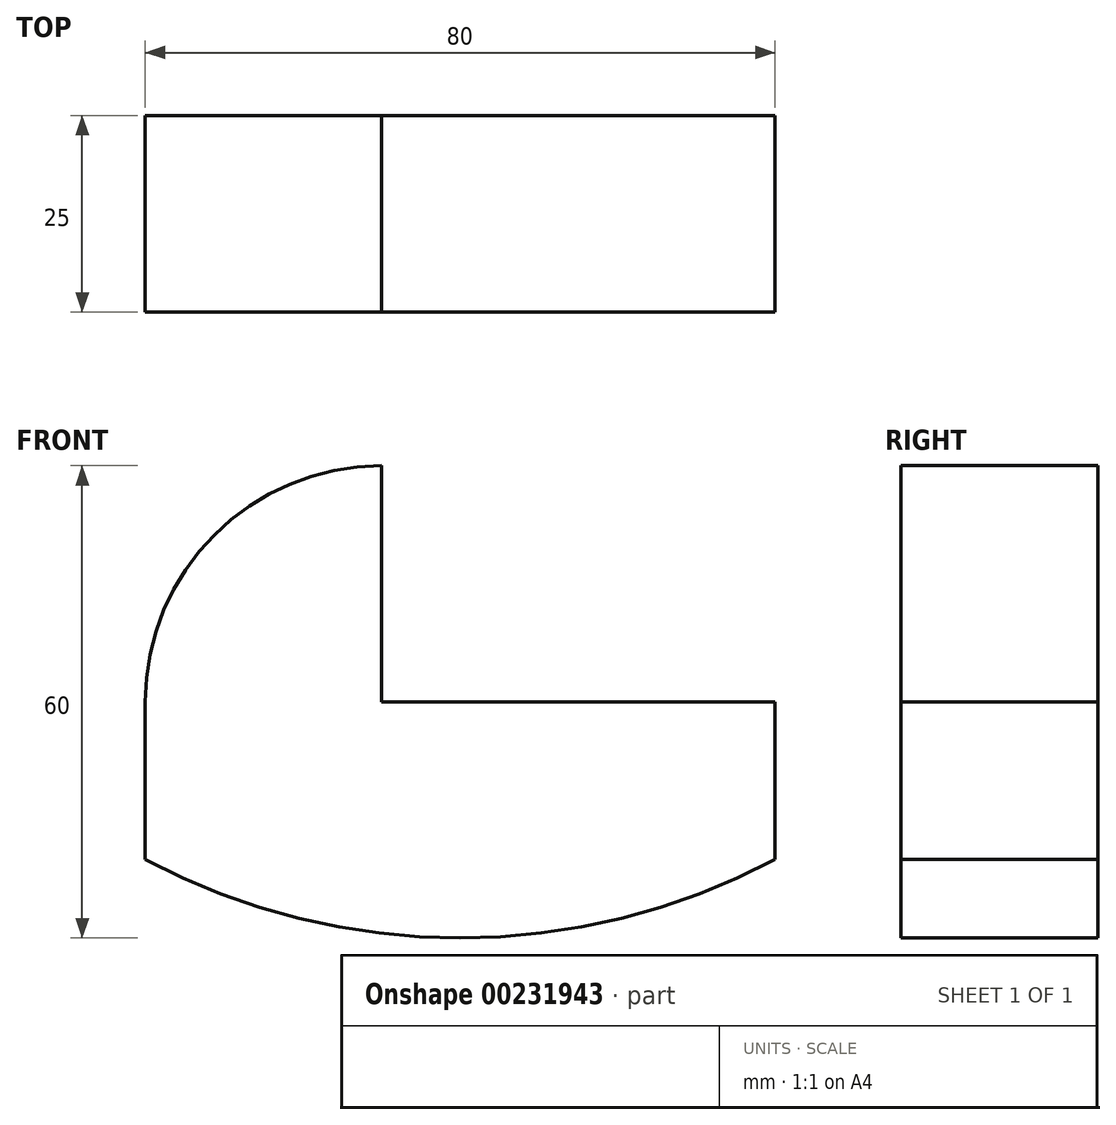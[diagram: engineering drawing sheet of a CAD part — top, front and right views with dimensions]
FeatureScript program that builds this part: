
annotation { "Feature Type Name" : "Feature", "Feature Type Description" : "" }
export const myFeature = defineFeature(function(context is Context, id is Id, definition is map)
    precondition{}
    {
        {
            var Q0;
            Q0=qCreatedBy(makeId("Front.planeOp"),FACE);
            var sketch = newSketch(context, id + "F0", { "sketchPlane" : qUnion([Q0])});
            skLineSegment(sketch, "E0", {"start": v(67.5, 0.98) * mm, "end": v(17.5, 0.98) * mm});
            skLineSegment(sketch, "E1", {"start": v(17.5, 0.98) * mm, "end": v(17.5, 30.98) * mm});
            skLineSegment(sketch, "E2", {"start": v(67.5, 0.98) * mm, "end": v(67.5, -19.02) * mm});
            skArc(sketch, "E3", {"start": v(-12.5, 0.98) * mm, "mid": v(-3.72, 22.2) * mm, "end": v(17.5, 30.98) * mm});
            skLineSegment(sketch, "E4", {"start": v(-12.5, 0.98) * mm, "end": v(-12.5, -19.02) * mm});
            skArc(sketch, "E5", {"start": v(-12.5, -19.02) * mm, "mid": v(27.5, -29.02) * mm, "end": v(67.5, -19.02) * mm});
            skSolve(sketch);
        }
        {
            var Q0;
            Q0=makeQuery(id+"F0.imprint","IMPRINT",FACE,{"disambiguationData":[TD([[makeQuery(id+"F0.imprint","IMPRINT",EDGE,{"derivedFrom":sQuery(id+"F0.wireOp",EDGE,"E0")}),1.0]])]});
            extrude(context, id + "F1", {"entities" : qUnion([Q0]), "depth" : 25 * mm});
        }
    });
